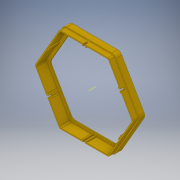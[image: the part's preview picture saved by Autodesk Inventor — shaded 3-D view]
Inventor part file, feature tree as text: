
AUTODESK INVENTOR PART (.ipt)
format: ipt  version: 2019 (Build 230136000, 136)  size: 307,712 bytes
history: native  units: mm
features: extrude x6, sketch x6, projected_geometry x4, fillet x2, other x1, pattern_circular x1
ambient origin geometry x8: Origin, YZ Plane, XZ Plane, XY Plane, X Axis, Y Axis, Z Axis, Center Point
bodies: Solid1 (feature_tree)
feature tree (20):
  extrude  "Extrusion1"  Depth=2.0mm
  extrude  "Extrusion5"  Depth=2.0mm
  extrude  "Extrusion6"  Depth=20.0mm
  fillet  "Fillet1"  [1 undecoded]
  fillet  "Fillet2"  Radius=6.0mm
  extrude  "Extrusion7"  TaperAngle=0.0deg  [1 undecoded]
  extrude  "Extrusion8"  Depth=4.0mm
  other  "Work Axis2"
  pattern_circular  "Circular Pattern1"  [2 undecoded]
  extrude  "Extrusion9"  Depth=6.5mm
  sketch  "Sketch1"  dims[d0=175.0mm d1=2.0mm]
  sketch  "Sketch5"  dims[d2=0.0mm d15=2.0mm]
  projected_geometry  "Projected Loop4"
  sketch  "Sketch7"  dims[d16=2.0mm d17=20.0mm d18=0.0mm d19=6.0mm]
  projected_geometry  "Projected Loop6"
  sketch  "Sketch8"  dims[d20=7.0mm d21=0.0mm]
  sketch  "Sketch9"  dims[d22=10.0mm d23=4.0mm]
  projected_geometry  "Projected Loop7"
  sketch  "Sketch11"  dims[d24=10.0mm d25=3.3mm d26=6.5mm d27=0.0mm d28=4.0mm d29=3.0mm d30=5.0mm d31=0.0mm d32=60.0mm d33=360.0deg d35=10.0mm d36=0.0mm]
  projected_geometry  "Projected Loop8"
note: 4 required parameter values undecoded (feature->parameter linkage not recoverable at this tier; creation-order binding heuristic only, values carry confidence <= 0.55)
